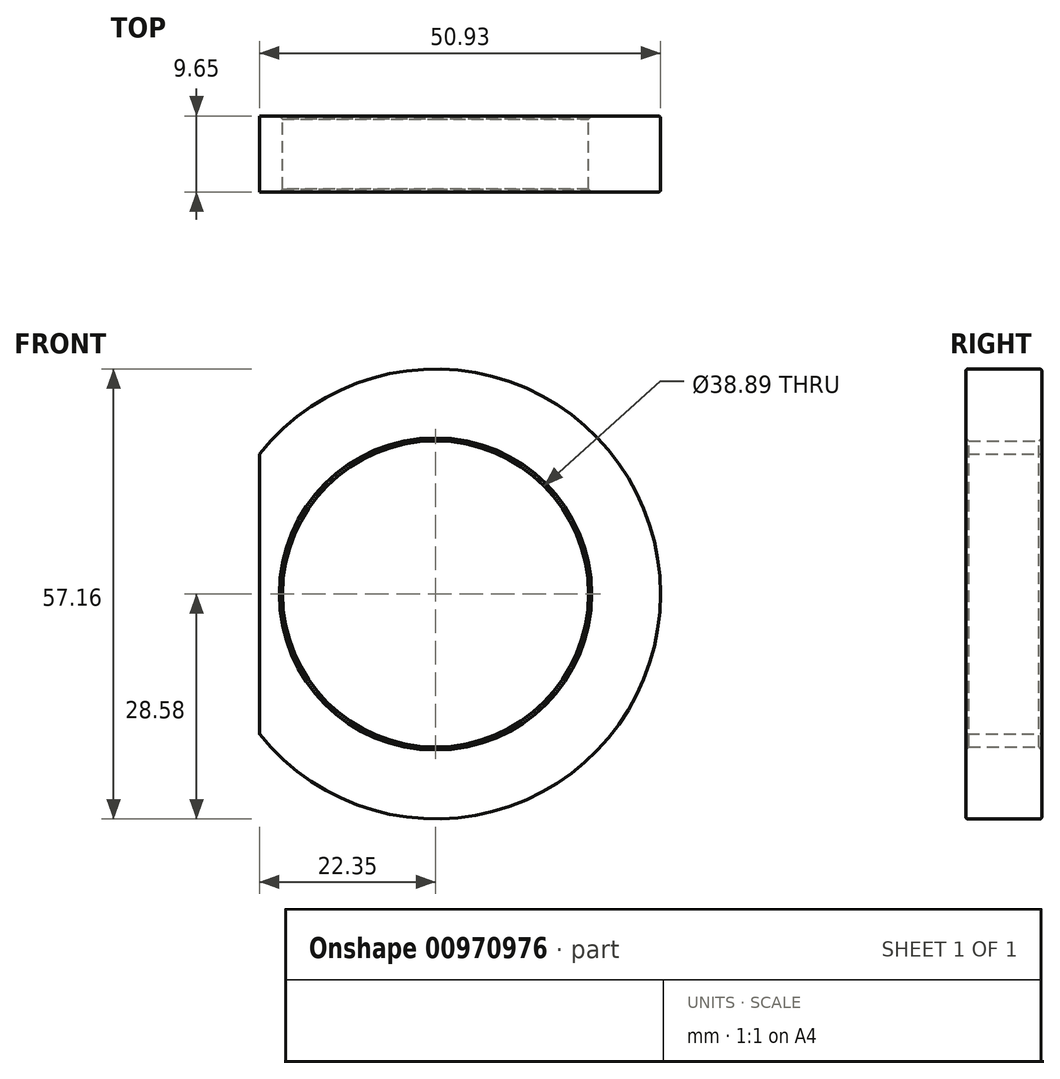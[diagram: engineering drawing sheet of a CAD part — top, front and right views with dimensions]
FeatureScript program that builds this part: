
annotation { "Feature Type Name" : "Feature", "Feature Type Description" : "" }
export const myFeature = defineFeature(function(context is Context, id is Id, definition is map)
    precondition{}
    {
        {
            var Q0;
            Q0=qCreatedBy(makeId("Front.planeOp"),FACE);
            var sketch = newSketch(context, id + "F0", { "sketchPlane" : qUnion([Q0])});
            skArc(sketch, "E0", {"start": v(-22.35, -17.8) * mm, "mid": v(28.58, 0) * mm, "end": v(-22.35, 17.8) * mm});
            skCircle(sketch, "E1", {"center": v(0, 0) * mm, "radius": 19.44 * mm});
            skLineSegment(sketch, "E2", {"start": v(-22.35, 17.8) * mm, "end": v(-22.35, -17.8) * mm});
            skLineSegment(sketch, "E3", {"start": v(28.58, 0) * mm, "end": v(28.58, 32) * mm, "construction": true});
            skSolve(sketch);
        }
        {
            var Q0;
            Q0=makeQuery(id+"F0.imprint","IMPRINT",FACE,{"disambiguationData":[TD([[makeQuery(id+"F0.imprint","IMPRINT",EDGE,{"derivedFrom":sQuery(id+"F0.wireOp",EDGE,"E0")}),1.0]])]});
            extrude(context, id + "F1", {"entities" : qUnion([Q0]), "depth" : 9.65 * mm, "offsetDistance" : 25.4 * mm});
        }
        {
            var Q0;
            Q0=makeQuery(id+"F1.opExtrude","CAP_EDGE",EDGE,{"disambiguationData":[OSD([sQuery(id+"F0.wireOp",EDGE,"E1")])],"isStart":false});
            var Q1;
            Q1=makeQuery(id+"F1.opExtrude","CAP_EDGE",EDGE,{"disambiguationData":[OSD([sQuery(id+"F0.wireOp",EDGE,"E1")])],"isStart":true});
            chamfer(context, id + "F2", {"entities" : qUnion([Q0, Q1]), "width" : 0.38 * mm, "tangentPropagation" : true});
        }
        {
            var Q0;
            Q0=makeQuery(id+"F1.opExtrude","CAP_EDGE",EDGE,{"disambiguationData":[OSD([sQuery(id+"F0.wireOp",EDGE,"E0")])],"isStart":false});
            var Q1;
            Q1=makeQuery(id+"F1.opExtrude","CAP_EDGE",EDGE,{"disambiguationData":[OSD([sQuery(id+"F0.wireOp",EDGE,"E0")])],"isStart":true});
            fillet(context, id + "F3", {"entities" : qUnion([Q0, Q1]), "radius" : 0.25 * mm, "tangentPropagation" : true, "allowEdgeOverflow" : false});
        }
    });
